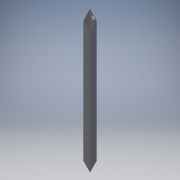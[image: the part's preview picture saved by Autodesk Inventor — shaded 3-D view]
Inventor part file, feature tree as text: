
AUTODESK INVENTOR PART (.ipt)
format: ipt  version: 2016 (Build 200138000, 138)  size: 118,272 bytes
history: native  units: in
note: dims shown in document units (in); Inventor stores cm internally (conversion verified against a paired STEP export)
features: extrude x4, sketch x4
ambient origin geometry x8: Origin, YZ Plane, XZ Plane, XY Plane, X Axis, Y Axis, Z Axis, Center Point
bodies: Solid1 (feature_tree)
feature tree (8):
  extrude  "Extrusion1"  Depth=1.0in
  extrude  "Extrusion2"  Depth=20.0in TaperAngle=0.0deg
  extrude  "Extrusion5"  Depth=1.5in
  extrude  "Extrusion6"  Depth=1.0in
  sketch  "Sketch1"  dims[d0=1.0in d1=1.0in]
  sketch  "Sketch2"  dims[d2=0.0625in d3=20.0in d4=0.0in]
  sketch  "Sketch5"  dims[d5=0.5in d6=1.5in]
  sketch  "Sketch6"  dims[d7=1.0in d8=0.0in d19=0.5in d20=0.535in d21=13.5in d22=1.0in d23=0.0in d24=0.5in d25=1.0in d26=0.0in]
